# Revit family: Vertical-Lift_Garaventa_Genesis-Shaftway
name_source: partatom
category: Specialty Equipment
units: mm (PartAtom-declared; Revit-internal decimal feet)

## family parameters
Always vertical = Yes
Classification Number = 23.50.05.11
Cut with Voids When Loaded = No
Enable Cutting in Views = No
Maintain Annotation Orientation = No
Part Type = Normal
Room Calculation Point = No
Round Connector Dimension = Use Diameter
Shared = No
Work Plane-Based = No

## types (1)
- Vertical-Lift_Garaventa_Genesis-Shaftway
    ADA Compliant = Yes
    Assembly Code = D1010310
    Building Code Conformance = [ASME A18.1; ASME A17.1; ASME A17.5; NFPA 70][CSA B355; CSA B44.1/ASME A17.5; CSA National Electrical Code]
    CL F R Doors = 40.000"
    CL Style Doors = 35.125"
    Capacity (Weight) = 750.00 lb
    Construction Details = http://www.arcat.com
    Default Elevation = 0.000"
    Description = Vertical Wheelchair lift - Type as Specified in the Contract Documents
    Expected Lifespan (Years) = 0
    Installation Phase = Interior fixtures and fittings
    Installation-Fabrication = http://www.garaventa.ca
    Keynote = 14425
    Lift Height = 120.000"
    Lift Operation = [10 fpm with Self-lubricating acme screw drive][17 fpm with Chain hydraulic]
    Low D Height = 80.000"
    Maintenance Schedule (Months) = 0
    Manufacturer = Garaventa Lift
    Manufacturer Fax = 604-594-9915
    Manufacturer Website = www.garaventa.ca
    Mast Height = 122.375"
    MasterFormat04 Keynote = 14 42 16
    Model = As Specified in the Contract Documents
    Platform Height = 42.125"
    Platform Length = 54.000"
    Platform Width = 36.000"
    Product Data = http://www.arcat.com
    Product Properties = http://www.arcat.com
    Sales Information = http://architects.garaventa.ca
    Send Message = http://admin.arcat.com
    Shaftway Length = 55.375"
    Shaftway Width = 55.125"
    SpecWizard = http://www.arcat.com
    Specification = http://www.arcat.com
    URL = www.garaventa.ca
    Warranty Duration (Years) = 1

## geometry (parser evidence)
native form markers: Blend x11, Sweep x3
no freeform markers — native parametric forms only
